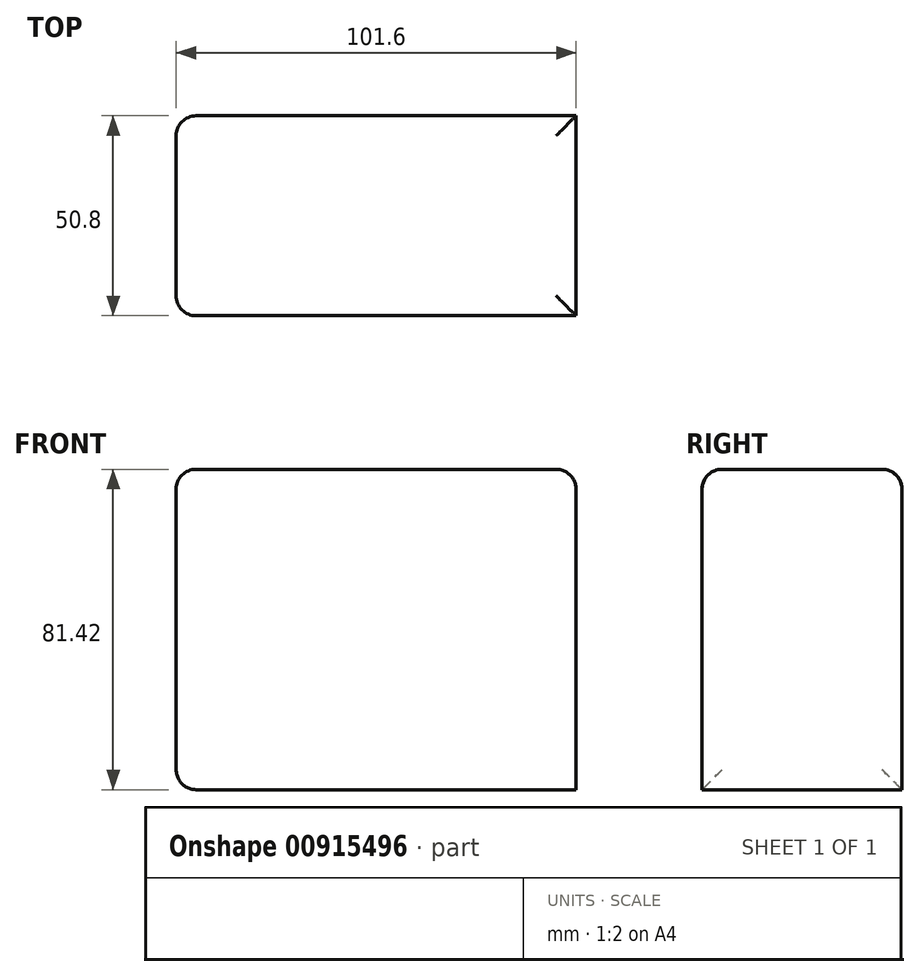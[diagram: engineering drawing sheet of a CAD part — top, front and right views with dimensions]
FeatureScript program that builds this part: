
annotation { "Feature Type Name" : "Feature", "Feature Type Description" : "" }
export const myFeature = defineFeature(function(context is Context, id is Id, definition is map)
    precondition{}
    {
        {
            var Q0;
            Q0=qCreatedBy(makeId("Front.planeOp"),FACE);
            var sketch = newSketch(context, id + "F0", { "sketchPlane" : qUnion([Q0])});
            skLineSegment(sketch, "E0.bottom", {"start": v(50.8, -52.04) * mm, "end": v(-50.8, -52.04) * mm});
            skLineSegment(sketch, "E0.top", {"start": v(50.8, 29.38) * mm, "end": v(-50.8, 29.38) * mm});
            skLineSegment(sketch, "E0.left", {"start": v(50.8, -52.04) * mm, "end": v(50.8, 29.38) * mm});
            skLineSegment(sketch, "E0.right", {"start": v(-50.8, -52.04) * mm, "end": v(-50.8, 29.38) * mm});
            skPoint(sketch, "E0.middle", {"position": v(0, -11.33) * mm});
            skSolve(sketch);
        }
        {
            var Q0;
            Q0=makeQuery(id+"F0.imprint","IMPRINT",FACE,{"disambiguationData":[TD([[makeQuery(id+"F0.imprint","IMPRINT",EDGE,{"derivedFrom":sQuery(id+"F0.wireOp",EDGE,"E0.bottom")}),-1.0]])]});
            extrude(context, id + "F1", {"entities" : qUnion([Q0]), "depth" : 50.8 * mm, "offsetDistance" : 25.4 * mm});
        }
        {
            var Q0;
            Q0=makeQuery(id+"F1.opExtrude","SWEPT_FACE",FACE,{"disambiguationData":[OSD([sQuery(id+"F0.wireOp",EDGE,"E0.right")])]});
            var Q1;
            Q1=makeQuery(id+"F1.opExtrude","SWEPT_EDGE",EDGE,{"disambiguationData":[OSD([sQuery(id+"F0.wireOp",EDGE,"E0.top"),sQuery(id+"F0.wireOp",EDGE,"E0.right")])]});
            var Q2;
            Q2=makeQuery(id+"F1.opExtrude","CAP_EDGE",EDGE,{"disambiguationData":[OSD([sQuery(id+"F0.wireOp",EDGE,"E0.top")])],"isStart":true});
            var Q3;
            Q3=makeQuery(id+"F1.opExtrude","CAP_EDGE",EDGE,{"disambiguationData":[OSD([sQuery(id+"F0.wireOp",EDGE,"E0.top")])],"isStart":false});
            var Q4;
            Q4=makeQuery(id+"F1.opExtrude","SWEPT_EDGE",EDGE,{"disambiguationData":[OSD([sQuery(id+"F0.wireOp",EDGE,"E0.top"),sQuery(id+"F0.wireOp",EDGE,"E0.left")])]});
            fillet(context, id + "F2", {"entities" : qUnion([Q0, Q1, Q2, Q3, Q4]), "radius" : 5.08 * mm, "tangentPropagation" : true, "allowEdgeOverflow" : false});
        }
    });
